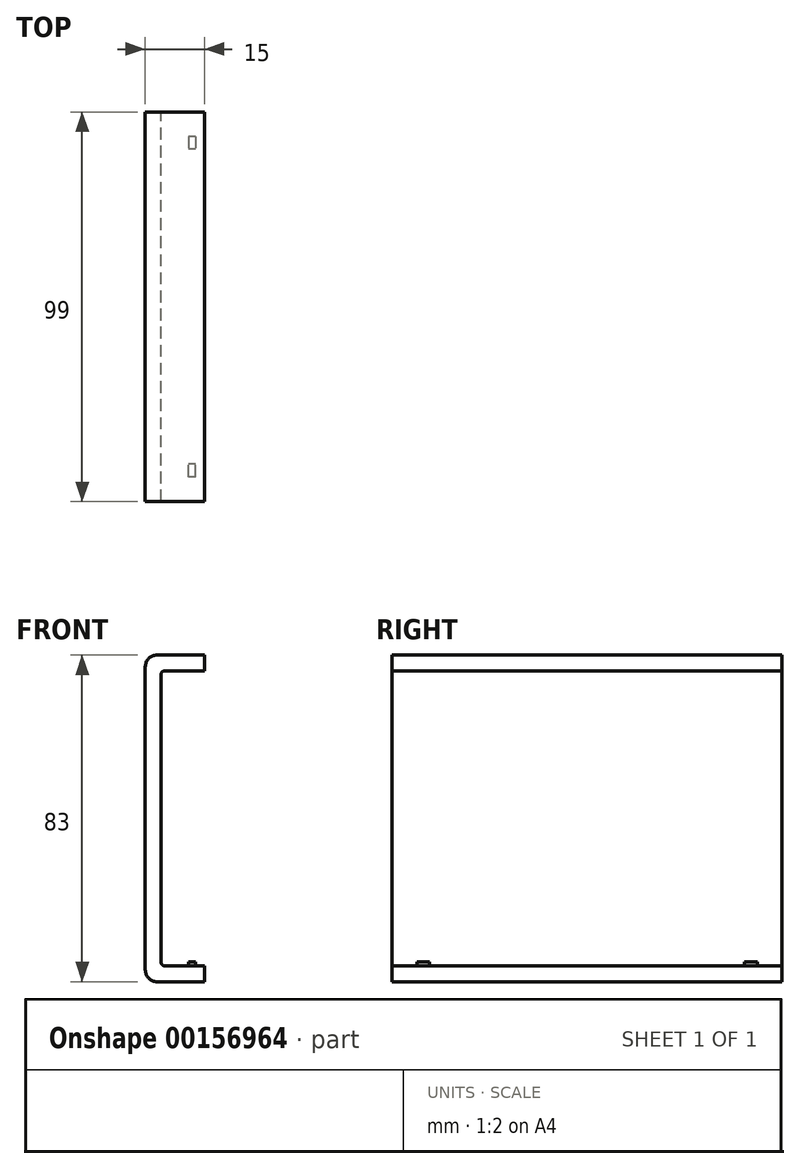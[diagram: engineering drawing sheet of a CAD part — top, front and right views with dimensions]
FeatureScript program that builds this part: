
annotation { "Feature Type Name" : "Feature", "Feature Type Description" : "" }
export const myFeature = defineFeature(function(context is Context, id is Id, definition is map)
    precondition{}
    {
        {
            var Q0;
            Q0=qCreatedBy(makeId("Front.planeOp"),FACE);
            var sketch = newSketch(context, id + "F0", { "sketchPlane" : qUnion([Q0])});
            skLineSegment(sketch, "E0", {"start": v(0, 38.75) * mm, "end": v(0, -38.25) * mm});
            skLineSegment(sketch, "E1", {"start": v(3, 41.75) * mm, "end": v(15, 41.75) * mm});
            skLineSegment(sketch, "E2", {"start": v(3, -41.25) * mm, "end": v(15, -41.25) * mm});
            skLineSegment(sketch, "E3", {"start": v(15, 41.75) * mm, "end": v(15, 37.75) * mm});
            skLineSegment(sketch, "E4", {"start": v(15, 37.75) * mm, "end": v(5, 37.75) * mm});
            skLineSegment(sketch, "E5", {"start": v(4, 36.75) * mm, "end": v(4, -36.25) * mm});
            skLineSegment(sketch, "E6", {"start": v(5, -37.25) * mm, "end": v(15, -37.25) * mm});
            skLineSegment(sketch, "E7", {"start": v(15, -37.25) * mm, "end": v(15, -41.25) * mm});
            skPoint(sketch, "E8.visualSharp", {"position": v(0, 41.75) * mm});
            skArc(sketch, "E8.filletArc", {"start": v(3, 41.75) * mm, "mid": v(0.88, 40.87) * mm, "end": v(0, 38.75) * mm});
            skPoint(sketch, "E9.visualSharp", {"position": v(0, -41.25) * mm});
            skArc(sketch, "E9.filletArc", {"start": v(0, -38.25) * mm, "mid": v(0.88, -40.37) * mm, "end": v(3, -41.25) * mm});
            skPoint(sketch, "E10.visualSharp", {"position": v(4, -37.25) * mm});
            skArc(sketch, "E10.filletArc", {"start": v(4, -36.25) * mm, "mid": v(4.3, -36.96) * mm, "end": v(5, -37.25) * mm});
            skPoint(sketch, "E11.visualSharp", {"position": v(4, 37.75) * mm});
            skArc(sketch, "E11.filletArc", {"start": v(5, 37.75) * mm, "mid": v(4.3, 37.46) * mm, "end": v(4, 36.75) * mm});
            skSolve(sketch);
        }
        {
            var Q0;
            Q0 = qSketchRegion(id + "F0", true);
            extrude(context, id + "F1", {"entities" : qUnion([Q0]), "depth" : 49.5 * mm, "hasSecondDirection" : true, "secondDirectionOppositeDirection" : true, "secondDirectionDepth" : 49.5 * mm});
        }
        {
            var Q0;
            Q0=makeQuery(id+"F1.opExtrude","SWEPT_FACE",FACE,{"disambiguationData":[OSD([sQuery(id+"F0.wireOp",EDGE,"E6")])]});
            var sketch = newSketch(context, id + "F2", { "sketchPlane" : qUnion([Q0])});
            skLineSegment(sketch, "E12.bottom", {"start": v(12.75, 43.25) * mm, "end": v(11, 43.25) * mm});
            skLineSegment(sketch, "E12.top", {"start": v(12.75, 40) * mm, "end": v(11, 40) * mm});
            skLineSegment(sketch, "E12.left", {"start": v(12.75, 43.25) * mm, "end": v(12.75, 40) * mm});
            skLineSegment(sketch, "E12.right", {"start": v(11, 43.25) * mm, "end": v(11, 40) * mm});
            skPoint(sketch, "E12.middle", {"position": v(11.88, 41.63) * mm});
            skLineSegment(sketch, "E13.MirrorCS", {"start": v(12.75, -43.25) * mm, "end": v(11, -43.25) * mm});
            skLineSegment(sketch, "E14.MirrorCS", {"start": v(12.75, -43.25) * mm, "end": v(12.75, -40) * mm});
            skLineSegment(sketch, "E15.MirrorCS", {"start": v(12.75, -40) * mm, "end": v(11, -40) * mm});
            skLineSegment(sketch, "E16.MirrorCS", {"start": v(11, -43.25) * mm, "end": v(11, -40) * mm});
            skPoint(sketch, "E17.MirrorP", {"position": v(11.88, -41.63) * mm});
            skSolve(sketch);
        }
        {
            var Q0;
            Q0 = qSketchRegion(id + "F2", true);
            extrude(context, id + "F3", {"entities" : qUnion([Q0]), "operationType" : NewBodyOperationType.ADD, "depth" : 1 * mm});
        }
    });
